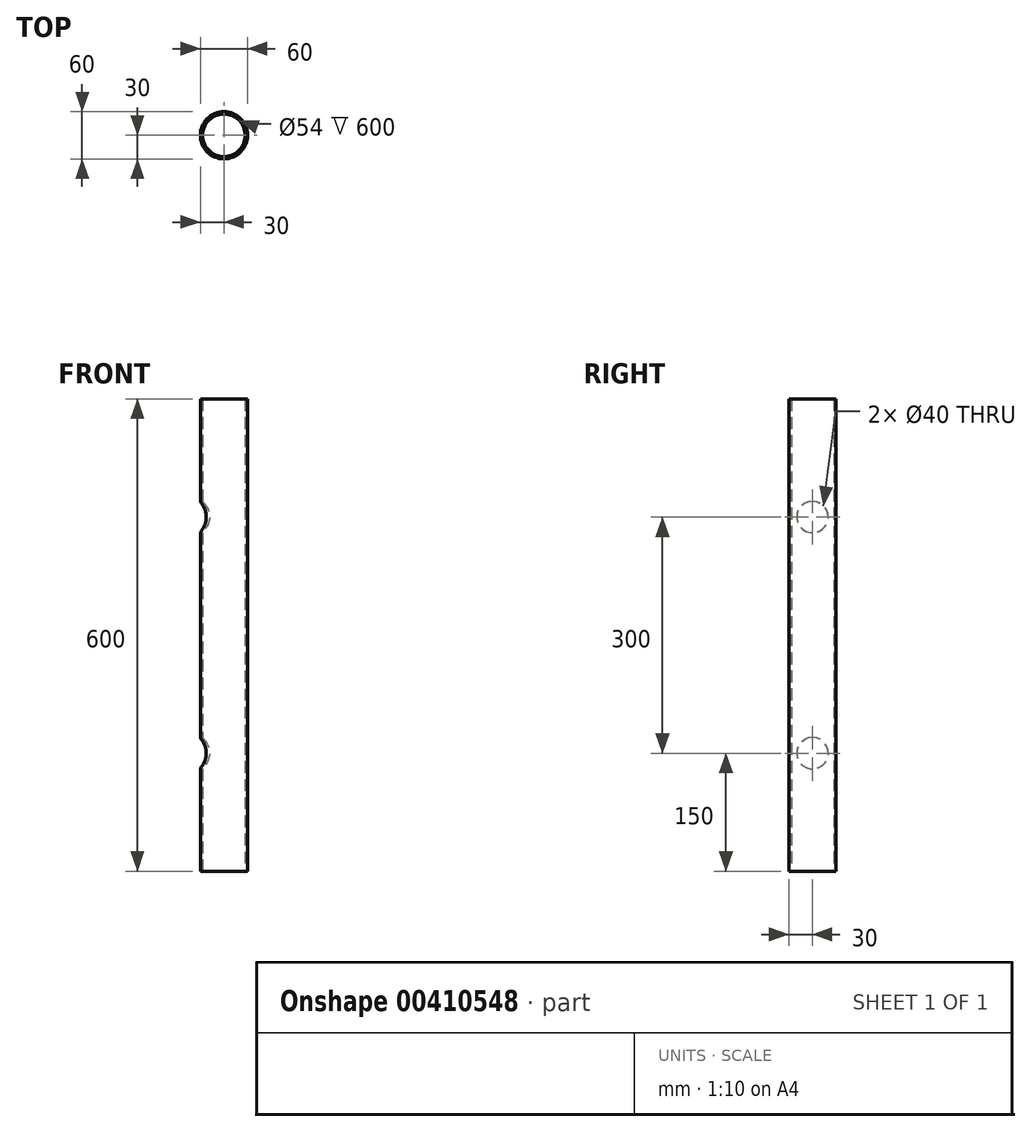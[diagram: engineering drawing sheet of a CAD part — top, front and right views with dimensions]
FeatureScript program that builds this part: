
annotation { "Feature Type Name" : "Feature", "Feature Type Description" : "" }
export const myFeature = defineFeature(function(context is Context, id is Id, definition is map)
    precondition{}
    {
        {
            var Q0;
            Q0=qCreatedBy(makeId("Top.planeOp"),FACE);
            var sketch = newSketch(context, id + "F0", { "sketchPlane" : qUnion([Q0])});
            skCircle(sketch, "E0", {"center": v(0, 0) * mm, "radius": 30 * mm});
            skCircle(sketch, "E1", {"center": v(0, 0) * mm, "radius": 27 * mm});
            skSolve(sketch);
        }
        {
            var Q0;
            Q0 = qSketchRegion(id + "F0", true);
            extrude(context, id + "F1", {"entities" : qUnion([Q0]), "depth" : 600 * mm});
        }
        {
            var Q0;
            Q0=qCreatedBy(makeId("Right.planeOp"),FACE);
            var sketch = newSketch(context, id + "F2", { "sketchPlane" : qUnion([Q0])});
            skCircle(sketch, "E2", {"center": v(0, 450) * mm, "radius": 20 * mm});
            skCircle(sketch, "E3", {"center": v(0, 150) * mm, "radius": 20 * mm});
            skSolve(sketch);
        }
        {
            var Q0;
            Q0 = qSketchRegion(id + "F2", true);
            extrude(context, id + "F3", {"entities" : qUnion([Q0]), "operationType" : NewBodyOperationType.REMOVE, "oppositeDirection" : true, "depth" : 50 * mm});
        }
        {
            var Q0;
            Q0=qCreatedBy(makeId("Right.planeOp"),FACE);
            var sketch = newSketch(context, id + "F4", { "sketchPlane" : qUnion([Q0])});
            skCircle(sketch, "E4.0", {"center": v(0, 150) * mm, "radius": 20 * mm});
            skCircle(sketch, "E5.0", {"center": v(0, 450) * mm, "radius": 20 * mm});
            skSolve(sketch);
        }
    });
